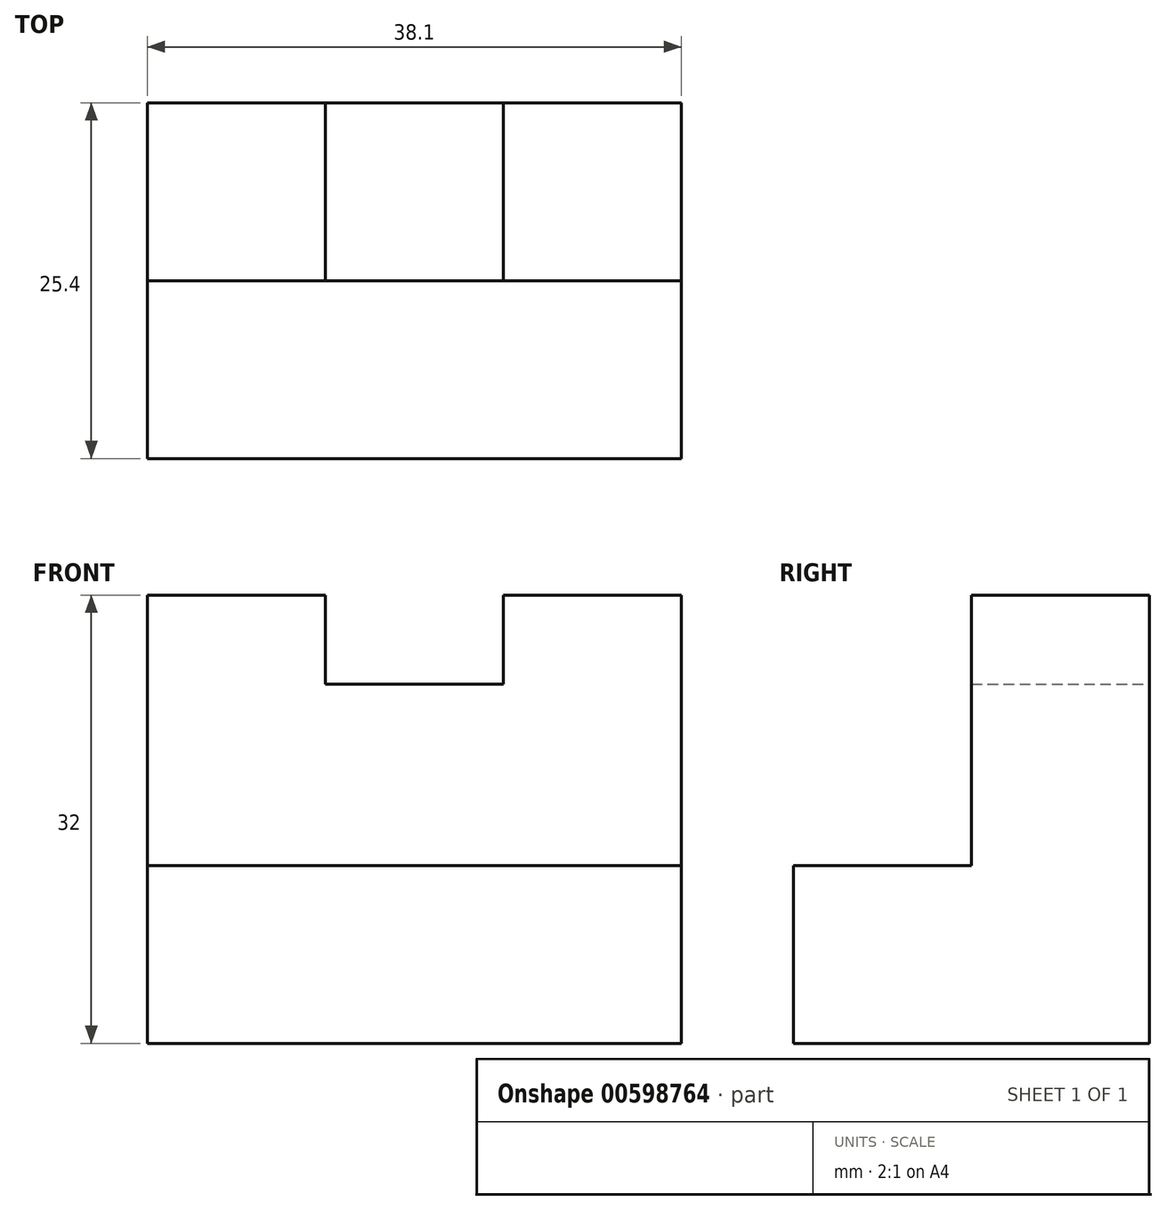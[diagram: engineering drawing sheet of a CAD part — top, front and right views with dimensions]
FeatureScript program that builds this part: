
annotation { "Feature Type Name" : "Feature", "Feature Type Description" : "" }
export const myFeature = defineFeature(function(context is Context, id is Id, definition is map)
    precondition{}
    {
        {
            var Q0;
            Q0=qCreatedBy(makeId("Front.planeOp"),FACE);
            var sketch = newSketch(context, id + "F0", { "sketchPlane" : qUnion([Q0])});
            skLineSegment(sketch, "E0", {"start": v(0, 0) * mm, "end": v(38.1, 0) * mm});
            skLineSegment(sketch, "E1", {"start": v(38.1, 0) * mm, "end": v(38.1, 12.7) * mm});
            skLineSegment(sketch, "E2", {"start": v(38.1, 12.7) * mm, "end": v(0, 12.7) * mm});
            skLineSegment(sketch, "E3", {"start": v(0, 12.7) * mm, "end": v(0, 0) * mm});
            skSolve(sketch);
        }
        {
            var Q0;
            Q0 = qSketchRegion(id + "F0", true);
            extrude(context, id + "F1", {"entities" : qUnion([Q0]), "depth" : 25.4 * mm, "offsetDistance" : 25.4 * mm});
        }
        {
            var Q0;
            Q0=qCreatedBy(makeId("Front.planeOp"),FACE);
            var sketch = newSketch(context, id + "F2", { "sketchPlane" : qUnion([Q0])});
            skLineSegment(sketch, "E4", {"start": v(0, 12.95) * mm, "end": v(0, 32) * mm});
            skLineSegment(sketch, "E5", {"start": v(0, 32) * mm, "end": v(12.7, 32) * mm});
            skLineSegment(sketch, "E6", {"start": v(12.7, 32) * mm, "end": v(12.7, 25.65) * mm});
            skLineSegment(sketch, "E7", {"start": v(12.7, 25.65) * mm, "end": v(25.4, 25.65) * mm});
            skLineSegment(sketch, "E8", {"start": v(25.4, 25.65) * mm, "end": v(25.4, 32) * mm});
            skLineSegment(sketch, "E9", {"start": v(25.4, 32) * mm, "end": v(38.1, 32) * mm});
            skLineSegment(sketch, "E10", {"start": v(38.1, 32) * mm, "end": v(38.1, 0) * mm});
            skLineSegment(sketch, "E11", {"start": v(38.1, 0) * mm, "end": v(0, 0) * mm});
            skLineSegment(sketch, "E12", {"start": v(0, 0) * mm, "end": v(0, 12.95) * mm});
            skSolve(sketch);
        }
        {
            var Q0;
            Q0 = qSketchRegion(id + "F2", true);
            extrude(context, id + "F3", {"entities" : qUnion([Q0]), "operationType" : NewBodyOperationType.ADD, "depth" : 12.7 * mm, "offsetDistance" : 25.4 * mm});
        }
    });
